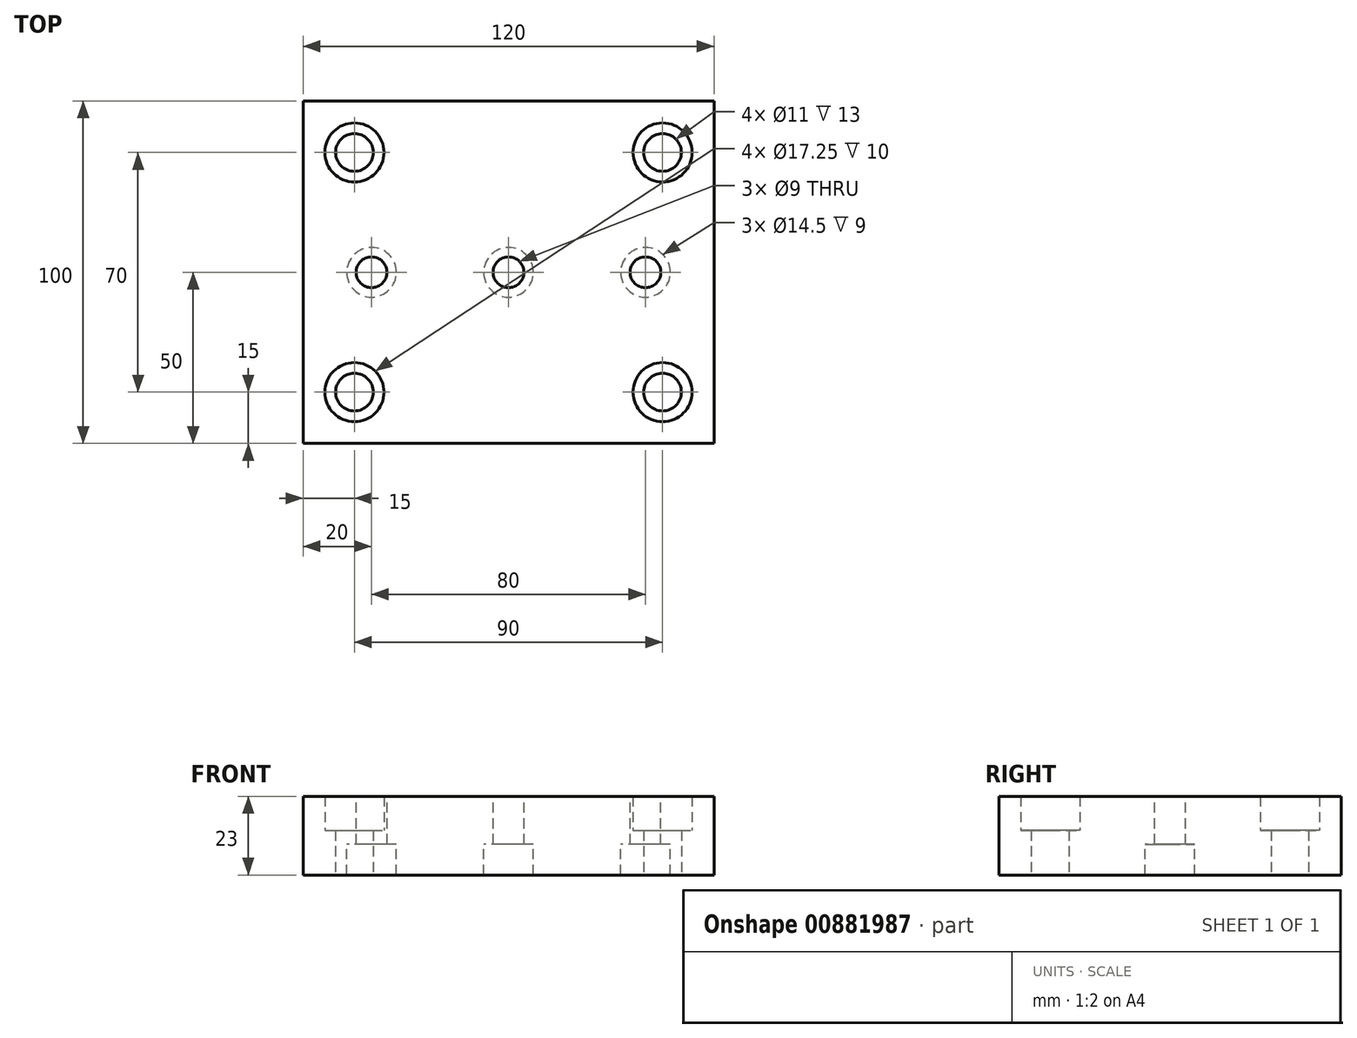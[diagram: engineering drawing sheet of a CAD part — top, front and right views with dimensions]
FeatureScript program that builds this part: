
annotation { "Feature Type Name" : "Feature", "Feature Type Description" : "" }
export const myFeature = defineFeature(function(context is Context, id is Id, definition is map)
    precondition{}
    {
        {
            var Q0;
            Q0=qCreatedBy(makeId("Top.planeOp"),FACE);
            var sketch = newSketch(context, id + "F0", { "sketchPlane" : qUnion([Q0])});
            skLineSegment(sketch, "E0.bottom", {"start": v(60, -50) * mm, "end": v(-60, -50) * mm});
            skLineSegment(sketch, "E0.top", {"start": v(60, 50) * mm, "end": v(-60, 50) * mm});
            skLineSegment(sketch, "E0.left", {"start": v(60, -50) * mm, "end": v(60, 50) * mm});
            skLineSegment(sketch, "E0.right", {"start": v(-60, -50) * mm, "end": v(-60, 50) * mm});
            skPoint(sketch, "E0.middle", {"position": v(0, 0) * mm});
            skSolve(sketch);
        }
        {
            var Q0;
            Q0 = qSketchRegion(id + "F0", true);
            extrude(context, id + "F1", {"entities" : qUnion([Q0]), "depth" : 23 * mm, "offsetDistance" : 25 * mm});
        }
        {
            var Q0;
            Q0=makeQuery(id+"F1.opExtrude","CAP_FACE",FACE,{"disambiguationData":[OSD([sQuery(id+"F0.wireOp",EDGE,"E0.bottom"),sQuery(id+"F0.wireOp",EDGE,"E0.top"),sQuery(id+"F0.wireOp",EDGE,"E0.left"),sQuery(id+"F0.wireOp",EDGE,"E0.right")])],"isStart":true});
            var sketch = newSketch(context, id + "F2", { "sketchPlane" : qUnion([Q0])});
            skPoint(sketch, "E1", {"position": v(-40, 0) * mm});
            skPoint(sketch, "E2", {"position": v(0, 0) * mm});
            skPoint(sketch, "E3", {"position": v(40, 0) * mm});
            skLineSegment(sketch, "E4", {"start": v(-60, 0) * mm, "end": v(-40, 0) * mm, "construction": true});
            skLineSegment(sketch, "E5", {"start": v(0, 0) * mm, "end": v(-40, 0) * mm, "construction": true});
            skLineSegment(sketch, "E6", {"start": v(0, 0) * mm, "end": v(40, 0) * mm, "construction": true});
            skSolve(sketch);
        }
        {
            var Q0;
            Q0=sQuery(id+"F2.wireOp",VERTEX,"E1");
            var Q1;
            Q1=sQuery(id+"F2.wireOp",VERTEX,"E2");
            var Q2;
            Q2=sQuery(id+"F2.wireOp",VERTEX,"E3");
            var Q3;
            Q3=makeQuery(id+"F1.opExtrude","SWEPT_BODY",BODY,{"disambiguationData":[OSD([sQuery(id+"F0.wireOp",EDGE,"E0.bottom"),sQuery(id+"F0.wireOp",EDGE,"E0.top"),sQuery(id+"F0.wireOp",EDGE,"E0.left"),sQuery(id+"F0.wireOp",EDGE,"E0.right")])]});
            hole(context, id + "F3", {"style" : HoleStyle.C_BORE, "endStyle" : HoleEndStyle.THROUGH, "holeDiameter" : 9 * mm, "cBoreDiameter" : 14.5 * mm, "cBoreDepth" : 9 * mm, "majorDiameter" : 6 * mm, "isTappedThrough" : true, "tappedDepth" : 12 * mm, "tapClearance" : 3, "locations" : qUnion([Q0, Q1, Q2]), "scope" : qUnion([Q3]), "startStyle" : HoleStartStyle.SKETCH});
        }
        {
            var Q0;
            Q0=makeQuery(id+"F1.opExtrude","CAP_FACE",FACE,{"disambiguationData":[OSD([sQuery(id+"F0.wireOp",EDGE,"E0.bottom"),sQuery(id+"F0.wireOp",EDGE,"E0.top"),sQuery(id+"F0.wireOp",EDGE,"E0.left"),sQuery(id+"F0.wireOp",EDGE,"E0.right")])],"isStart":false});
            var sketch = newSketch(context, id + "F4", { "sketchPlane" : qUnion([Q0])});
            skPoint(sketch, "E7", {"position": v(-45, 35) * mm});
            skPoint(sketch, "E8", {"position": v(-45, -35) * mm});
            skPoint(sketch, "E9", {"position": v(45, -35) * mm});
            skPoint(sketch, "E10", {"position": v(45, 35) * mm});
            skLineSegment(sketch, "E11.bottom", {"start": v(-45, 35) * mm, "end": v(45, 35) * mm, "construction": true});
            skLineSegment(sketch, "E11.top", {"start": v(-45, -35) * mm, "end": v(45, -35) * mm, "construction": true});
            skLineSegment(sketch, "E11.left", {"start": v(-45, 35) * mm, "end": v(-45, -35) * mm, "construction": true});
            skLineSegment(sketch, "E11.right", {"start": v(45, 35) * mm, "end": v(45, -35) * mm, "construction": true});
            skPoint(sketch, "E11.middle", {"position": v(0, 0) * mm});
            skSolve(sketch);
        }
        {
            var Q0;
            Q0=sQuery(id+"F4.wireOp",VERTEX,"E7");
            var Q1;
            Q1=sQuery(id+"F4.wireOp",VERTEX,"E10");
            var Q2;
            Q2=sQuery(id+"F4.wireOp",VERTEX,"E9");
            var Q3;
            Q3=sQuery(id+"F4.wireOp",VERTEX,"E8");
            var Q4;
            Q4=makeQuery(id+"F1.opExtrude","SWEPT_BODY",BODY,{"disambiguationData":[OSD([sQuery(id+"F0.wireOp",EDGE,"E0.bottom"),sQuery(id+"F0.wireOp",EDGE,"E0.top"),sQuery(id+"F0.wireOp",EDGE,"E0.left"),sQuery(id+"F0.wireOp",EDGE,"E0.right")])]});
            hole(context, id + "F5", {"style" : HoleStyle.C_BORE, "endStyle" : HoleEndStyle.THROUGH, "standardTappedOrClearance" : lookupTablePath({ "fit" : "Normal", "standard" : "ISO", "size" : "M10", "type" : "Clearance" }), "standardBlindInLast" : lookupTablePath({ "fit" : "Normal", "standard" : "ISO", "size" : "M10", "type" : "Clearance" }), "holeDiameter" : 11 * mm, "cBoreDiameter" : 17.25 * mm, "cBoreDepth" : 10 * mm, "majorDiameter" : 5 * mm, "isTappedThrough" : true, "tappedDepth" : 12 * mm, "tapClearance" : 3, "locations" : qUnion([Q0, Q1, Q2, Q3]), "scope" : qUnion([Q4]), "startStyle" : HoleStartStyle.SKETCH});
        }
    });
